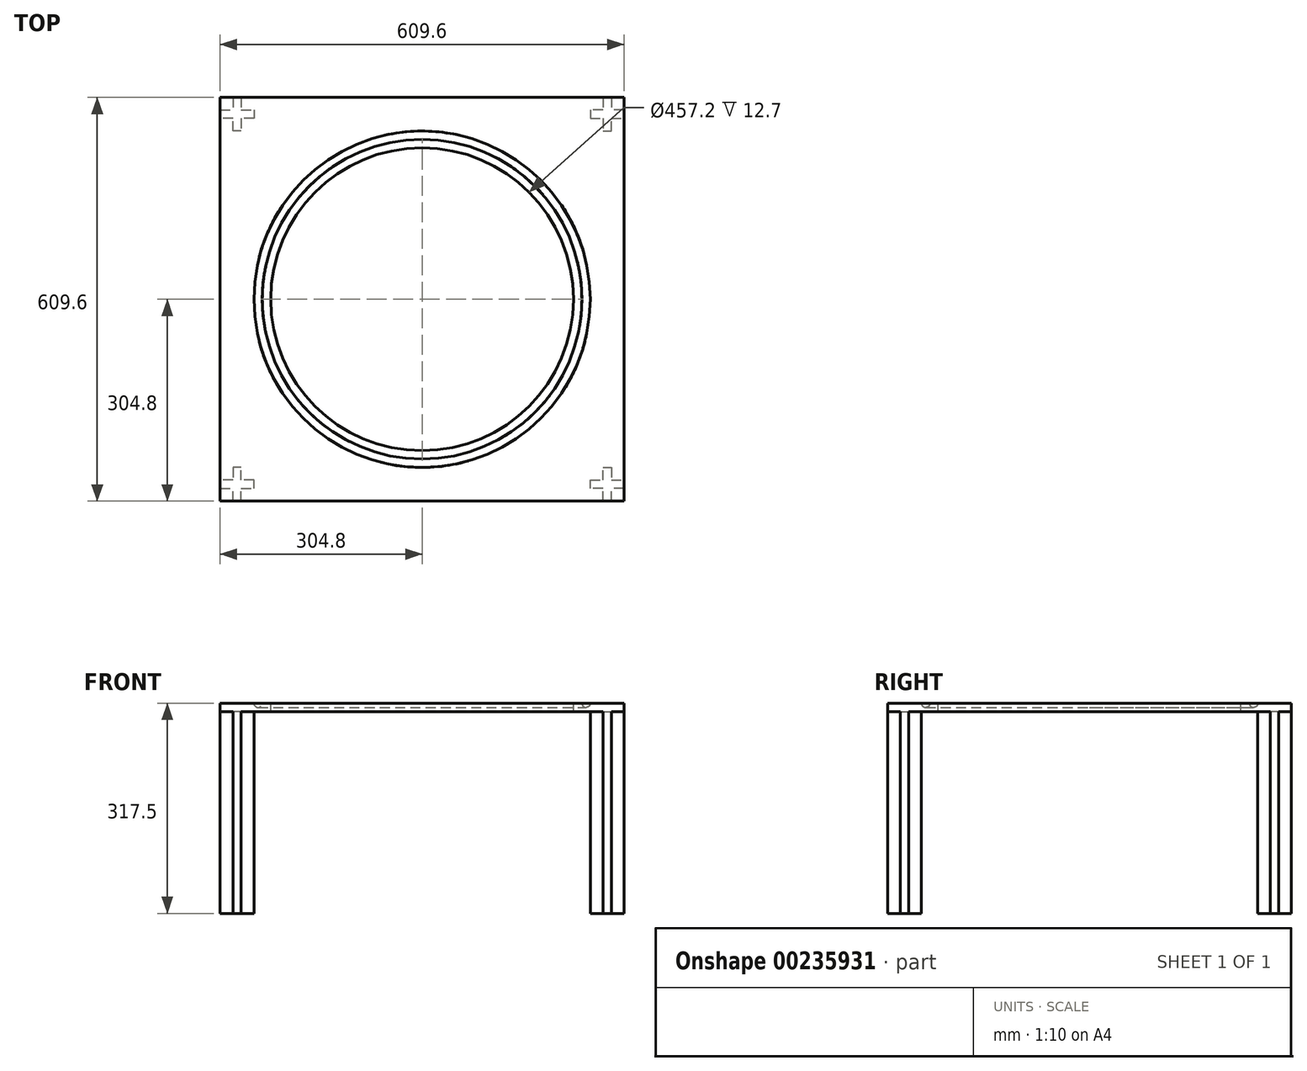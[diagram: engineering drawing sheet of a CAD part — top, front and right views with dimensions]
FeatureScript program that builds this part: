
annotation { "Feature Type Name" : "Feature", "Feature Type Description" : "" }
export const myFeature = defineFeature(function(context is Context, id is Id, definition is map)
    precondition{}
    {
        {
            var Q0;
            Q0=qCreatedBy(makeId("Top.planeOp"),FACE);
            var sketch = newSketch(context, id + "F0", { "sketchPlane" : qUnion([Q0])});
            skLineSegment(sketch, "E0.bottom", {"start": v(0, 0) * mm, "end": v(609.6, 0) * mm});
            skLineSegment(sketch, "E0.top", {"start": v(0, 609.6) * mm, "end": v(609.6, 609.6) * mm});
            skLineSegment(sketch, "E0.left", {"start": v(0, 0) * mm, "end": v(0, 609.6) * mm});
            skLineSegment(sketch, "E0.right", {"start": v(609.6, 0) * mm, "end": v(609.6, 609.6) * mm});
            skSolve(sketch);
        }
        {
            var Q0;
            Q0=makeQuery(id+"F0.imprint","IMPRINT",FACE,{"disambiguationData":[TD([[makeQuery(id+"F0.imprint","IMPRINT",EDGE,{"derivedFrom":sQuery(id+"F0.wireOp",EDGE,"E0.bottom")}),1.0]])]});
            extrude(context, id + "F1", {"entities" : qUnion([Q0]), "endBound" : BoundingType.SYMMETRIC, "depth" : 12.7 * mm});
        }
        {
            var Q0;
            Q0=makeQuery(id+"F1.opExtrude","CAP_FACE",FACE,{"disambiguationData":[OSD([sQuery(id+"F0.wireOp",EDGE,"E0.bottom"),sQuery(id+"F0.wireOp",EDGE,"E0.top"),sQuery(id+"F0.wireOp",EDGE,"E0.left"),sQuery(id+"F0.wireOp",EDGE,"E0.right")])],"isStart":true});
            var sketch = newSketch(context, id + "F2", { "sketchPlane" : qUnion([Q0])});
            skLineSegment(sketch, "E1", {"start": v(304.8, 0) * mm, "end": v(304.8, -609.6) * mm, "construction": true});
            skLineSegment(sketch, "E2", {"start": v(609.6, -304.8) * mm, "end": v(0, -304.8) * mm, "construction": true});
            skLineSegment(sketch, "E3.top", {"start": v(0, -19.05) * mm, "end": v(19.05, -19.05) * mm});
            skLineSegment(sketch, "E3.right", {"start": v(19.05, 0) * mm, "end": v(19.05, -19.05) * mm});
            skLineSegment(sketch, "E4", {"start": v(19.05, 0) * mm, "end": v(31.75, 0) * mm});
            skLineSegment(sketch, "E5", {"start": v(31.75, 0) * mm, "end": v(31.75, -19.05) * mm});
            skLineSegment(sketch, "E6", {"start": v(31.75, -19.05) * mm, "end": v(50.8, -19.05) * mm});
            skLineSegment(sketch, "E7", {"start": v(50.8, -19.05) * mm, "end": v(50.8, -31.75) * mm});
            skLineSegment(sketch, "E8", {"start": v(50.8, -31.75) * mm, "end": v(31.75, -31.75) * mm});
            skLineSegment(sketch, "E9", {"start": v(31.75, -31.75) * mm, "end": v(31.75, -50.8) * mm});
            skLineSegment(sketch, "E10", {"start": v(31.75, -50.8) * mm, "end": v(19.05, -50.8) * mm});
            skLineSegment(sketch, "E11", {"start": v(19.05, -50.8) * mm, "end": v(19.05, -31.75) * mm});
            skLineSegment(sketch, "E12", {"start": v(19.05, -31.75) * mm, "end": v(0, -31.75) * mm});
            skLineSegment(sketch, "E13", {"start": v(0, -31.75) * mm, "end": v(0, -19.05) * mm});
            skLineSegment(sketch, "E14.MirrorCS", {"start": v(590.55, -31.75) * mm, "end": v(609.6, -31.75) * mm});
            skLineSegment(sketch, "E15.MirrorCS", {"start": v(590.55, -50.8) * mm, "end": v(590.55, -31.75) * mm});
            skLineSegment(sketch, "E16.MirrorCS", {"start": v(558.8, -19.05) * mm, "end": v(558.8, -31.75) * mm});
            skLineSegment(sketch, "E17.MirrorCS", {"start": v(577.85, -31.75) * mm, "end": v(577.85, -50.8) * mm});
            skLineSegment(sketch, "E18.MirrorCS", {"start": v(577.85, -19.05) * mm, "end": v(558.8, -19.05) * mm});
            skLineSegment(sketch, "E19.MirrorCS", {"start": v(558.8, -31.75) * mm, "end": v(577.85, -31.75) * mm});
            skLineSegment(sketch, "E20.MirrorCS", {"start": v(590.55, 0) * mm, "end": v(577.85, 0) * mm});
            skLineSegment(sketch, "E21.MirrorCS", {"start": v(577.85, -50.8) * mm, "end": v(590.55, -50.8) * mm});
            skLineSegment(sketch, "E22.MirrorCS", {"start": v(590.55, 0) * mm, "end": v(590.55, -19.05) * mm});
            skLineSegment(sketch, "E23.MirrorCS", {"start": v(609.6, -31.75) * mm, "end": v(609.6, -19.05) * mm});
            skLineSegment(sketch, "E24.MirrorCS", {"start": v(609.6, -19.05) * mm, "end": v(590.55, -19.05) * mm});
            skLineSegment(sketch, "E25.MirrorCS", {"start": v(577.85, 0) * mm, "end": v(577.85, -19.05) * mm});
            skLineSegment(sketch, "E26.MirrorCS", {"start": v(19.05, -609.6) * mm, "end": v(31.75, -609.6) * mm});
            skLineSegment(sketch, "E27.MirrorCS", {"start": v(590.55, -609.6) * mm, "end": v(577.85, -609.6) * mm});
            skLineSegment(sketch, "E28.MirrorCS", {"start": v(558.8, -590.55) * mm, "end": v(558.8, -577.85) * mm});
            skLineSegment(sketch, "E29.MirrorCS", {"start": v(0, -577.85) * mm, "end": v(0, -590.55) * mm});
            skLineSegment(sketch, "E30.MirrorCS", {"start": v(577.85, -558.8) * mm, "end": v(590.55, -558.8) * mm});
            skLineSegment(sketch, "E31.MirrorCS", {"start": v(31.75, -558.8) * mm, "end": v(19.05, -558.8) * mm});
            skLineSegment(sketch, "E32.MirrorCS", {"start": v(50.8, -590.55) * mm, "end": v(50.8, -577.85) * mm});
            skLineSegment(sketch, "E33.MirrorCS", {"start": v(609.6, -577.85) * mm, "end": v(609.6, -590.55) * mm});
            skLineSegment(sketch, "E34.MirrorCS", {"start": v(31.75, -590.55) * mm, "end": v(50.8, -590.55) * mm});
            skLineSegment(sketch, "E35.MirrorCS", {"start": v(31.75, -609.6) * mm, "end": v(31.75, -590.55) * mm});
            skLineSegment(sketch, "E36.MirrorCS", {"start": v(19.05, -609.6) * mm, "end": v(19.05, -590.55) * mm});
            skLineSegment(sketch, "E37.MirrorCS", {"start": v(0, -590.55) * mm, "end": v(19.05, -590.55) * mm});
            skLineSegment(sketch, "E38.MirrorCS", {"start": v(590.55, -558.8) * mm, "end": v(590.55, -577.85) * mm});
            skLineSegment(sketch, "E39.MirrorCS", {"start": v(590.55, -577.85) * mm, "end": v(609.6, -577.85) * mm});
            skLineSegment(sketch, "E40.MirrorCS", {"start": v(19.05, -558.8) * mm, "end": v(19.05, -577.85) * mm});
            skLineSegment(sketch, "E41.MirrorCS", {"start": v(577.85, -577.85) * mm, "end": v(577.85, -558.8) * mm});
            skLineSegment(sketch, "E42.MirrorCS", {"start": v(590.55, -609.6) * mm, "end": v(590.55, -590.55) * mm});
            skLineSegment(sketch, "E43.MirrorCS", {"start": v(577.85, -590.55) * mm, "end": v(558.8, -590.55) * mm});
            skLineSegment(sketch, "E44.MirrorCS", {"start": v(577.85, -609.6) * mm, "end": v(577.85, -590.55) * mm});
            skLineSegment(sketch, "E45.MirrorCS", {"start": v(609.6, -590.55) * mm, "end": v(590.55, -590.55) * mm});
            skLineSegment(sketch, "E46.MirrorCS", {"start": v(19.05, -577.85) * mm, "end": v(0, -577.85) * mm});
            skLineSegment(sketch, "E47.MirrorCS", {"start": v(31.75, -577.85) * mm, "end": v(31.75, -558.8) * mm});
            skLineSegment(sketch, "E48.MirrorCS", {"start": v(50.8, -577.85) * mm, "end": v(31.75, -577.85) * mm});
            skLineSegment(sketch, "E49.MirrorCS", {"start": v(558.8, -577.85) * mm, "end": v(577.85, -577.85) * mm});
            skSolve(sketch);
        }
        {
            var Q0;
            Q0 = qSketchRegion(id + "F2", true);
            extrude(context, id + "F3", {"entities" : qUnion([Q0]), "operationType" : NewBodyOperationType.ADD, "depth" : 304.8 * mm});
        }
        {
            var Q0;
            Q0=makeQuery(id+"F1.opExtrude","CAP_FACE",FACE,{"disambiguationData":[OSD([sQuery(id+"F0.wireOp",EDGE,"E0.bottom"),sQuery(id+"F0.wireOp",EDGE,"E0.top"),sQuery(id+"F0.wireOp",EDGE,"E0.left"),sQuery(id+"F0.wireOp",EDGE,"E0.right")])],"isStart":false});
            var sketch = newSketch(context, id + "F4", { "sketchPlane" : qUnion([Q0])});
            skLineSegment(sketch, "E50", {"start": v(304.8, 609.6) * mm, "end": v(304.8, 304.8) * mm, "construction": true});
            skLineSegment(sketch, "E51", {"start": v(304.8, 304.8) * mm, "end": v(0, 304.8) * mm, "construction": true});
            skPoint(sketch, "E52.orphan", {"position": v(304.8, 0) * mm});
            skPoint(sketch, "E53.orphan", {"position": v(609.6, 304.8) * mm});
            skPoint(sketch, "E54", {"position": v(304.8, 304.8) * mm});
            skCircle(sketch, "E55", {"center": v(304.8, 304.8) * mm, "radius": 228.6 * mm});
            skCircle(sketch, "E56", {"center": v(304.8, 304.8) * mm, "radius": 241.3 * mm});
            skCircle(sketch, "E57", {"center": v(304.8, 304.8) * mm, "radius": 254 * mm});
            skSolve(sketch);
        }
        {
            var Q0;
            Q0=qCreatedBy(makeId("Front.planeOp"),FACE);
            cPlane(context, id + "F5", {"entities" : qUnion([Q0]), "cplaneType" : CPlaneType.OFFSET, "offset" : 304.8 * mm, "oppositeDirection" : true, "width" : 152.4 * mm, "height" : 152.4 * mm});
        }
        {
            var Q0;
            Q0=qCreatedBy(id+"F5.planeOp",FACE);
            var sketch = newSketch(context, id + "F6", { "sketchPlane" : qUnion([Q0])});
            skArc(sketch, "E58", {"start": v(50.8, 6.35) * mm, "mid": v(57.15, -0.16) * mm, "end": v(63.5, 6.35) * mm});
            skPoint(sketch, "E58.third.point", {"position": v(55.73, 0) * mm});
            skLineSegment(sketch, "E59", {"start": v(50.8, 6.35) * mm, "end": v(63.5, 6.35) * mm});
            skPoint(sketch, "E60.0", {"position": v(304.8, -6.35) * mm});
            skPoint(sketch, "E61.0", {"position": v(304.8, 6.35) * mm});
            skLineSegment(sketch, "E62", {"start": v(304.8, 6.35) * mm, "end": v(304.8, -6.35) * mm, "construction": true});
            skSolve(sketch);
        }
        {
            var Q0;
            Q0 = qSketchRegion(id + "F6", true);
            var Q1;
            Q1 = qConstructionFilter(qBodyType(qCreatedBy(id + "F6" ,EDGE), BodyType.WIRE), ConstructionObject.NO);
            var Q2;
            Q2=sQuery(id+"F6.wireOp",EDGE,"E62");
            revolve(context, id + "F7", {"operationType" : NewBodyOperationType.REMOVE, "entities" : qUnion([Q0]), "surfaceEntities" : qUnion([Q1]), "axis" : qUnion([Q2]), "revolveType" : RevolveType.FULL, "oppositeDirection" : true});
        }
        {
            var Q0;
            Q0=makeQuery(id+"F4.imprint","IMPRINT",FACE,{"disambiguationData":[TD([[makeQuery(id+"F4.imprint","IMPRINT",EDGE,{"derivedFrom":sQuery(id+"F4.wireOp",EDGE,"E55")}),1.0]])]});
            extrude(context, id + "F8", {"entities" : qUnion([Q0]), "operationType" : NewBodyOperationType.REMOVE, "endBound" : BoundingType.THROUGH_ALL, "oppositeDirection" : true, "depth" : 25.4 * mm});
        }
    });
